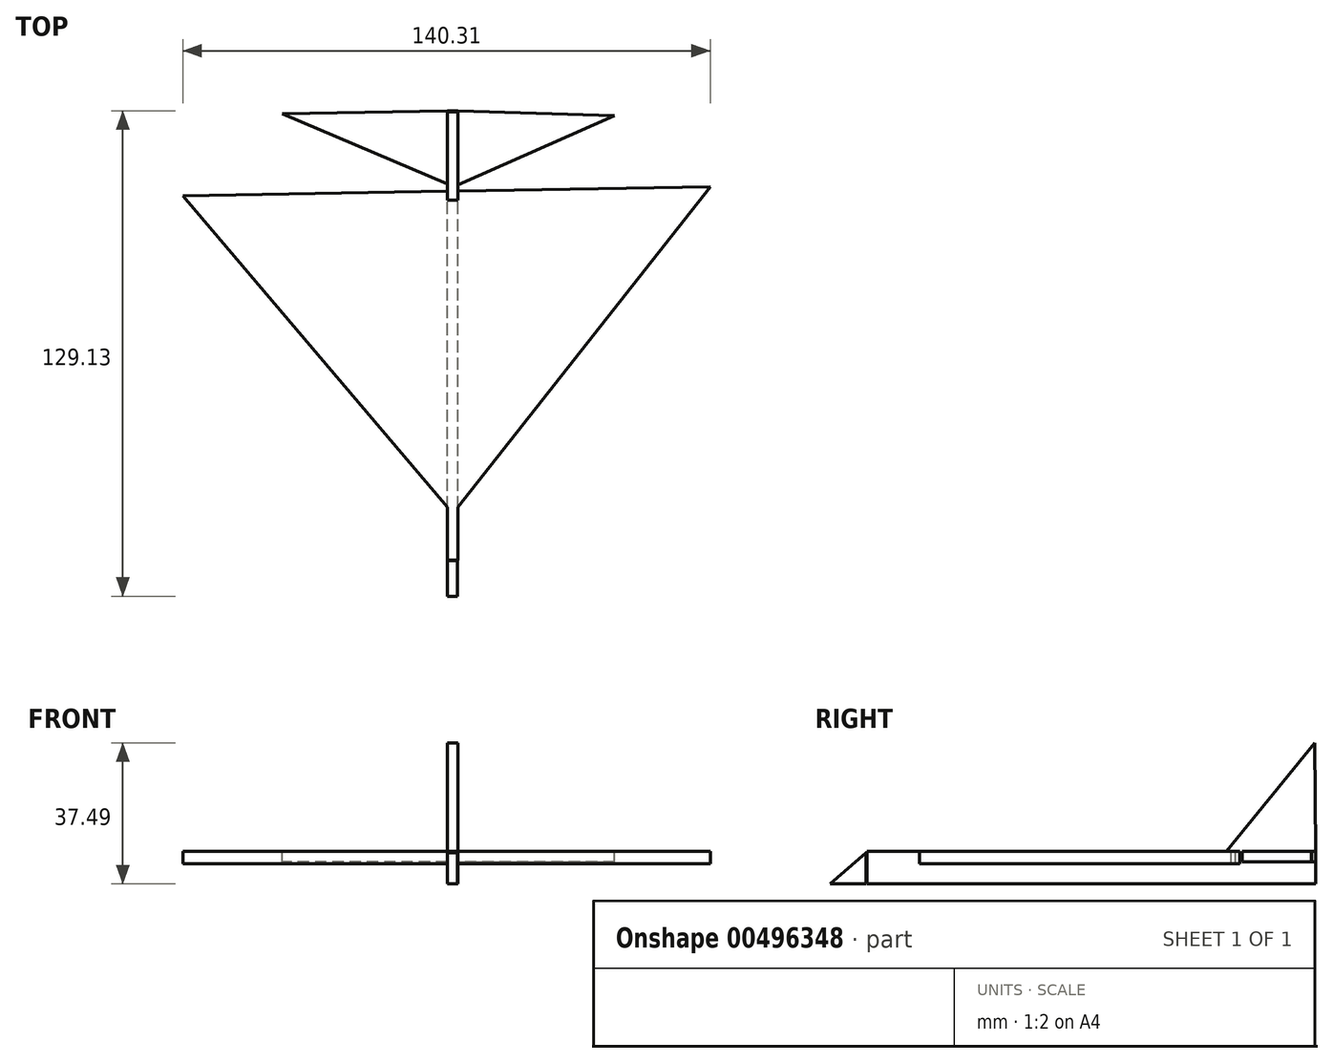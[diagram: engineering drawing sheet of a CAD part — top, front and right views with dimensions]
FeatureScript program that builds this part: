
annotation { "Feature Type Name" : "Feature", "Feature Type Description" : "" }
export const myFeature = defineFeature(function(context is Context, id is Id, definition is map)
    precondition{}
    {
        {
            var Q0;
            Q0=qCreatedBy(makeId("Right.planeOp"),FACE);
            var sketch = newSketch(context, id + "F0", { "sketchPlane" : qUnion([Q0])});
            skLineSegment(sketch, "E0.bottom", {"start": v(-57.07, 8.67) * mm, "end": v(62.39, 8.67) * mm});
            skLineSegment(sketch, "E0.top", {"start": v(-57.07, 0) * mm, "end": v(62.39, 0) * mm});
            skLineSegment(sketch, "E0.left", {"start": v(-57.07, 8.67) * mm, "end": v(-57.07, 0) * mm});
            skLineSegment(sketch, "E0.right", {"start": v(62.39, 8.67) * mm, "end": v(62.39, 0) * mm});
            skSolve(sketch);
        }
        {
            var Q0;
            Q0=qCreatedBy(makeId("Right.planeOp"),FACE);
            var sketch = newSketch(context, id + "F1", { "sketchPlane" : qUnion([Q0])});
            skLineSegment(sketch, "E1", {"start": v(-57.3, 8.27) * mm, "end": v(-66.74, 0) * mm});
            skLineSegment(sketch, "E2", {"start": v(-66.74, 0) * mm, "end": v(-57.3, 0) * mm});
            skLineSegment(sketch, "E3", {"start": v(-57.3, 0) * mm, "end": v(-57.3, 8.27) * mm});
            skSolve(sketch);
        }
        {
            var Q0;
            Q0=makeQuery(id+"F0.imprint","IMPRINT",FACE,{"disambiguationData":[TD([[makeQuery(id+"F0.imprint","IMPRINT",EDGE,{"derivedFrom":sQuery(id+"F0.wireOp",EDGE,"E0.bottom")}),-1.0]])]});
            extrude(context, id + "F2", {"entities" : qUnion([Q0]), "depth" : 2.8 * mm});
        }
        {
            var Q0;
            Q0=makeQuery(id+"F1.imprint","IMPRINT",FACE,{"disambiguationData":[TD([[makeQuery(id+"F1.imprint","IMPRINT",EDGE,{"derivedFrom":sQuery(id+"F1.wireOp",EDGE,"E1")}),1.0]])]});
            extrude(context, id + "F3", {"entities" : qUnion([Q0]), "depth" : 2.67 * mm});
        }
        {
            var Q0;
            Q0=makeQuery(id+"F2.opExtrude","SWEPT_FACE",FACE,{"disambiguationData":[OSD([sQuery(id+"F0.wireOp",EDGE,"E0.bottom")])]});
            var sketch = newSketch(context, id + "F4", { "sketchPlane" : qUnion([Q0])});
            skLineSegment(sketch, "E4", {"start": v(0, 42.97) * mm, "end": v(-43.86, 61.66) * mm});
            skLineSegment(sketch, "E5", {"start": v(-43.86, 61.66) * mm, "end": v(0, 62.39) * mm});
            skLineSegment(sketch, "E6", {"start": v(0, 62.39) * mm, "end": v(0, 42.97) * mm});
            skSolve(sketch);
        }
        {
            var Q0;
            Q0=makeQuery(id+"F2.opExtrude","CAP_FACE",FACE,{"disambiguationData":[OSD([sQuery(id+"F0.wireOp",EDGE,"E0.bottom"),sQuery(id+"F0.wireOp",EDGE,"E0.top"),sQuery(id+"F0.wireOp",EDGE,"E0.left"),sQuery(id+"F0.wireOp",EDGE,"E0.right")])],"isStart":false});
            var sketch = newSketch(context, id + "F5", { "sketchPlane" : qUnion([Q0])});
            skLineSegment(sketch, "E7", {"start": v(38.6, 8.67) * mm, "end": v(62.1, 37.49) * mm});
            skLineSegment(sketch, "E8", {"start": v(62.1, 37.49) * mm, "end": v(62.39, 8.67) * mm});
            skLineSegment(sketch, "E9", {"start": v(62.39, 8.67) * mm, "end": v(38.6, 8.67) * mm});
            skSolve(sketch);
        }
        {
            var Q0;
            {var subQ3=sQuery(id+"F4.wireOp",EDGE,"E6");Q0=makeQuery(id+"F4.imprint","IMPRINT",FACE,{"disambiguationData":[TD([[makeQuery(id+"F4.imprint","IMPRINT",EDGE,{"derivedFrom":subQ3}),-1.0]])]});}
            var sketch = newSketch(context, id + "F6", { "sketchPlane" : qUnion([Q0])});
            skLineSegment(sketch, "E10", {"start": v(2.8, 42.75) * mm, "end": v(44.5, 61.18) * mm});
            skLineSegment(sketch, "E11", {"start": v(44.5, 61.18) * mm, "end": v(2.84, 62.37) * mm});
            skLineSegment(sketch, "E12", {"start": v(2.84, 62.37) * mm, "end": v(2.8, 42.75) * mm});
            skSolve(sketch);
        }
        {
            var Q0;
            {var subQ3=sQuery(id+"F4.wireOp",EDGE,"E6");Q0=makeQuery(id+"F4.imprint","IMPRINT",FACE,{"disambiguationData":[TD([[makeQuery(id+"F4.imprint","IMPRINT",EDGE,{"derivedFrom":subQ3}),-1.0]])]});}
            var sketch = newSketch(context, id + "F7", { "sketchPlane" : qUnion([Q0])});
            skLineSegment(sketch, "E13", {"start": v(2.86, -43.08) * mm, "end": v(69.93, 42.2) * mm});
            skLineSegment(sketch, "E14", {"start": v(69.93, 42.2) * mm, "end": v(-70.38, 39.83) * mm});
            skLineSegment(sketch, "E15", {"start": v(-70.38, 39.83) * mm, "end": v(0, -43.08) * mm});
            skLineSegment(sketch, "E16", {"start": v(0, -43.08) * mm, "end": v(2.86, -43.08) * mm});
            skSolve(sketch);
        }
        {
            var Q0;
            {var subQ0=sQuery(id+"F7.wireOp",EDGE,"E13");Q0=makeQuery(id+"F7.imprint","IMPRINT",FACE,{"disambiguationData":[TD([[makeQuery(id+"F7.imprint","IMPRINT",EDGE,{"derivedFrom":subQ0}),1.0]])]});}
            var Q1;
            {var subQ0=sQuery(id+"F7.wireOp",EDGE,"E15");Q1=makeQuery(id+"F7.imprint","IMPRINT",FACE,{"disambiguationData":[TD([[makeQuery(id+"F7.imprint","IMPRINT",EDGE,{"derivedFrom":subQ0}),1.0]])]});}
            extrude(context, id + "F8", {"entities" : qUnion([Q0, Q1]), "operationType" : NewBodyOperationType.ADD, "oppositeDirection" : true, "depth" : 3.3 * mm});
        }
        {
            var Q0;
            Q0=makeQuery(id+"F6.imprint","IMPRINT",FACE,{"disambiguationData":[TD([[makeQuery(id+"F6.imprint","IMPRINT",EDGE,{"derivedFrom":sQuery(id+"F6.wireOp",EDGE,"E10")}),1.0]])]});
            var Q1;
            Q1=makeQuery(id+"F4.imprint","IMPRINT",FACE,{"disambiguationData":[TD([[makeQuery(id+"F4.imprint","IMPRINT",EDGE,{"derivedFrom":sQuery(id+"F4.wireOp",EDGE,"E4")}),-1.0]])]});
            extrude(context, id + "F9", {"entities" : qUnion([Q0, Q1]), "operationType" : NewBodyOperationType.ADD, "oppositeDirection" : true, "depth" : 2.8 * mm});
        }
        {
            var Q0;
            Q0=makeQuery(id+"F5.imprint","IMPRINT",FACE,{"disambiguationData":[TD([[makeQuery(id+"F5.imprint","IMPRINT",EDGE,{"derivedFrom":sQuery(id+"F5.wireOp",EDGE,"E7")}),-1.0]])]});
            extrude(context, id + "F10", {"entities" : qUnion([Q0]), "operationType" : NewBodyOperationType.ADD, "oppositeDirection" : true, "depth" : 2.8 * mm});
        }
    });
